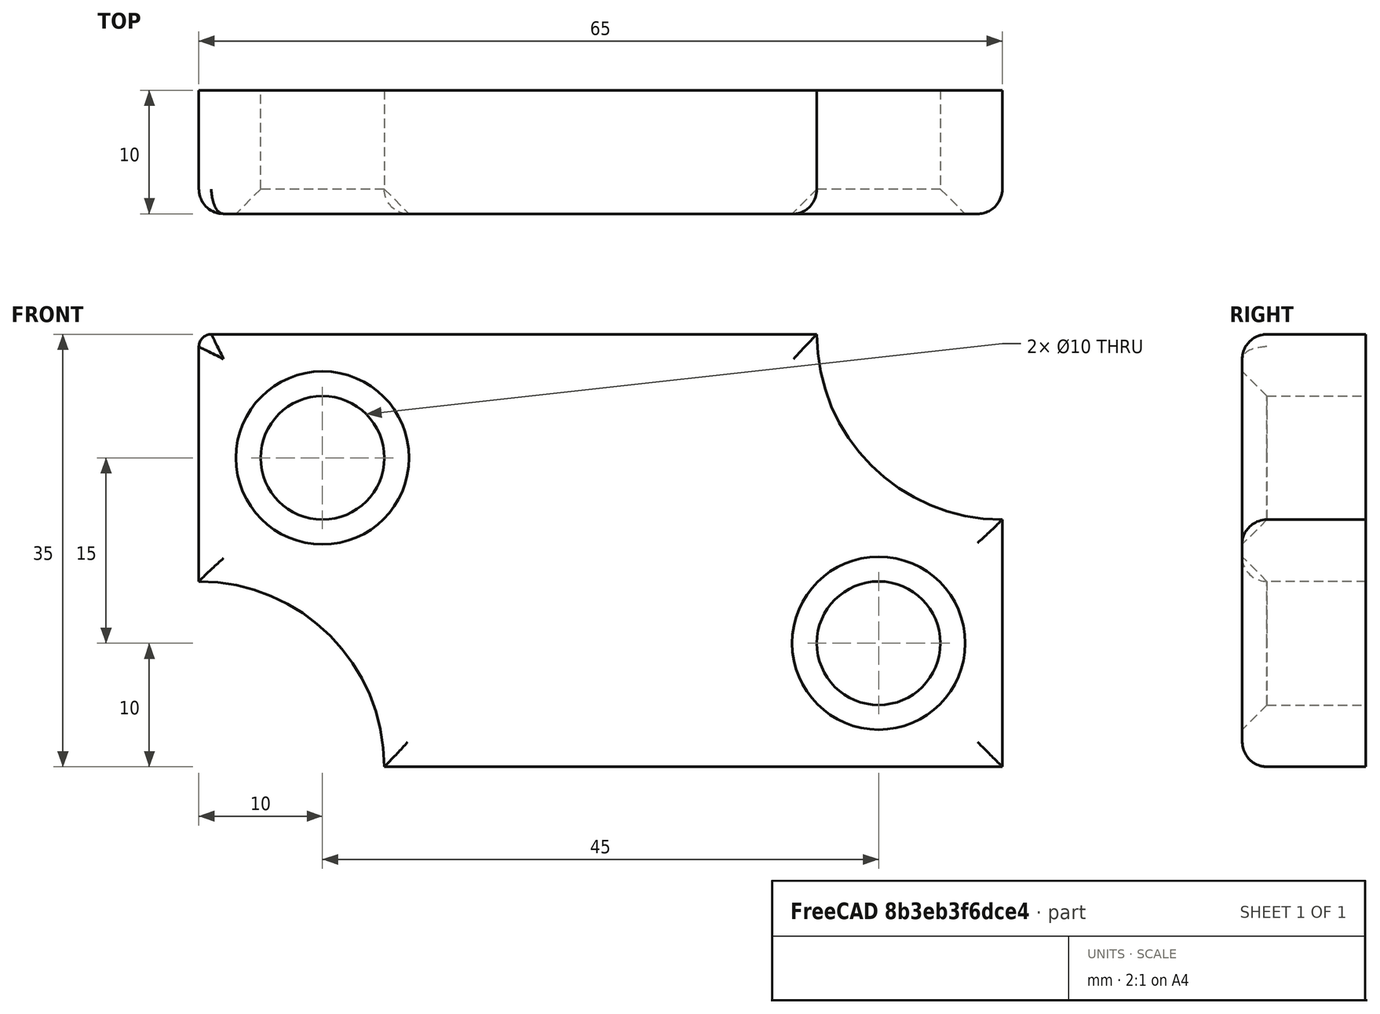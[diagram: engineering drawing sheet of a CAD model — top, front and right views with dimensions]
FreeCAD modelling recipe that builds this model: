
FCSTD DOCUMENT  (FreeCAD 0.20R29177 +426 (Git))
Label: Ejemplo 2 Pieza (Croquis)
License: All rights reserved
LicenseURL: http://en.wikipedia.org/wiki/All_rights_reserved
objects: Sketcher::SketchObject×2, PartDesign::Fillet×2, PartDesign::Pad×1, PartDesign::Chamfer×1, PartDesign::Body×1
note: 11 computed .brp shape members not serialized (recipe doc carries the construction recipe); baked Part::Feature solids carry a one-line shape summary decoded from their .brp

FEATURE [Sketcher::SketchObject] Sketch
  FullyConstrained = true
  MapMode = 5
  Placement = pos=(0,0,0) rot=(1,0,0;1.5708rad)
  Support = -> [XZ_Plane]
  sketch-geometry (8):
    g0: LineSegment StartX=9e-16 StartY=35 StartZ=0 EndX=50 EndY=35 EndZ=0
    g1: LineSegment StartX=65 StartY=20 StartZ=0 EndX=65 EndY=0 EndZ=0
    g2: LineSegment StartX=65 StartY=0 StartZ=0 EndX=15 EndY=0 EndZ=0
    g3: LineSegment StartX=9e-16 StartY=15 StartZ=0 EndX=9e-16 EndY=35 EndZ=0
    g4: ArcOfCircle CenterX=0 CenterY=0 CenterZ=0 NormalX=0 NormalY=0 NormalZ=1 AngleXU=0 Radius=15 StartAngle=0 EndAngle=1.5708
    g5: ArcOfCircle CenterX=65 CenterY=35 CenterZ=0 NormalX=0 NormalY=0 NormalZ=1 AngleXU=0 Radius=15 StartAngle=3.14159 EndAngle=4.71239
    g6: Circle CenterX=10 CenterY=25 CenterZ=0 NormalX=0 NormalY=0 NormalZ=1 AngleXU=0 Radius=5
    g7: Circle CenterX=55 CenterY=10 CenterZ=0 NormalX=0 NormalY=0 NormalZ=1 AngleXU=0 Radius=5
  constraints (25):
    c: Coincident(g1,g2)
    c: Coincident(g3,g0)
    c: Horizontal(g0)
    c: Horizontal(g2)
    c: Vertical(g1)
    c: Vertical(g3)
    c: Coincident(g4,g-1)
    c: Radius(g5) = 15
    c: Radius(g4) = 15
    c: Coincident(g0,g5)
    c: Coincident(g1,g5)
    c: Coincident(g2,g4)
    c: Coincident(g3,g4)
    c: PointOnObject(g0,g-2)
    c: PointOnObject(g1,g-1)
    c: DistanceY(g1,g1) = 20
    c: DistanceY(g3,g3) = 20
    c: DistanceX(g0,g0) = 50
    c: DistanceX(g2,g2) = 50
    c: Radius(g6) = 5
    c: DistanceX(g0,g6) = 10
    c: DistanceY(g6,g0) = 10
    c: Radius(g7) = 5
    c: DistanceY(g1,g7) = 10
    c: DistanceX(g7,g1) = 10
FEATURE [PartDesign::Pad] Pad
  Direction = (0,-1,2e-16)
  Length = 10
  Length2 = 10
  Placement = pos=(0,0,0) rot=(1,0,0;1.5708rad)
  Profile = -> Sketch
  ReferenceAxis = -> Sketch [N_Axis]
  Type = 0
FEATURE [PartDesign::Chamfer] Chamfer
  Angle = 45
  Base = -> Pad [Edge24,Edge21]
  BaseFeature = -> Pad
  ChamferType = 0
  FlipDirection = false
  Placement = pos=(0,0,0) rot=(1,0,0;1.5708rad)
  Size = 2
  Size2 = 1
  SupportTransform = false
  UseAllEdges = false
FEATURE [PartDesign::Fillet] Fillet
  Base = -> Chamfer [Edge16,Edge17,Edge19,Edge14,Edge15,Edge18]
  BaseFeature = -> Chamfer
  Placement = pos=(0,0,0) rot=(1,0,0;1.5708rad)
  Radius = 2
  SupportTransform = false
  UseAllEdges = false
FEATURE [PartDesign::Fillet] Fillet001
  Base = -> Fillet [Edge32]
  BaseFeature = -> Fillet
  Placement = pos=(0,0,0) rot=(1,0,0;1.5708rad)
  Radius = 1
  SupportTransform = false
  UseAllEdges = false
FEATURE [Sketcher::SketchObject] Sketch001
  FullyConstrained = false
  MapMode = 5
  Placement = pos=(0,-10,2.2e-15) rot=(1,0,0;1.5708rad)
  Support = -> [Fillet001]
  sketch-geometry (12):
    g0: LineSegment StartX=27.117 StartY=24.449 StartZ=0 EndX=32.0912 EndY=24.449 EndZ=0
    g1: LineSegment StartX=32.0912 StartY=24.449 StartZ=0 EndX=32.0912 EndY=19.6829 EndZ=0
    g2: LineSegment StartX=32.0912 StartY=19.6829 StartZ=0 EndX=36.4141 EndY=19.6829 EndZ=0
    g3: LineSegment StartX=36.4141 StartY=19.6829 StartZ=0 EndX=36.4141 EndY=15.0768 EndZ=0
    g4: LineSegment StartX=36.4141 StartY=15.0768 StartZ=0 EndX=32.3918 EndY=15.0768 EndZ=0
    g5: LineSegment StartX=32.3918 StartY=15.0768 StartZ=0 EndX=32.3918 EndY=9.89424 EndZ=0
    g6: LineSegment StartX=32.3918 StartY=9.89424 StartZ=0 EndX=27.4176 EndY=9.89424 EndZ=0
    g7: LineSegment StartX=27.4176 StartY=9.89424 StartZ=0 EndX=27.4176 EndY=15.0768 EndZ=0
    g8: LineSegment StartX=27.4176 StartY=15.0768 StartZ=0 EndX=22.7775 EndY=15.0768 EndZ=0
    g9: LineSegment StartX=22.7775 StartY=15.0768 StartZ=0 EndX=22.7775 EndY=19.6829 EndZ=0
    g10: LineSegment StartX=22.7775 StartY=19.6829 StartZ=0 EndX=27.117 EndY=19.6829 EndZ=0
    g11: LineSegment StartX=27.117 StartY=19.6829 StartZ=0 EndX=27.117 EndY=24.449 EndZ=0
  constraints (27):
    c: Horizontal(g0)
    c: Coincident(g0,g1)
    c: Vertical(g1)
    c: Coincident(g1,g2)
    c: Horizontal(g2)
    c: Coincident(g2,g3)
    c: Vertical(g3)
    c: Coincident(g3,g4)
    c: Coincident(g4,g5)
    c: Vertical(g5)
    c: Coincident(g5,g6)
    c: Horizontal(g6)
    c: Coincident(g6,g7)
    c: Vertical(g7)
    c: Coincident(g7,g8)
    c: Coincident(g8,g9)
    c: Coincident(g9,g10)
    c: Horizontal(g10)
    c: Coincident(g10,g11)
    c: Coincident(g11,g0)
    c: Vertical(g11)
    c: Equal(g9,g3)
    c: Equal(g6,g0)
    c: Equal(g1,g11)
    c: Vertical(g9)
    c: Horizontal(g4)
    c: Horizontal(g8)
FEATURE [PartDesign::Body] Body
  Group = -> [Sketch,Pad,Chamfer,Fillet,Fillet001,Sketch001]
  Origin = -> Origin
  Tip = -> Fillet001
